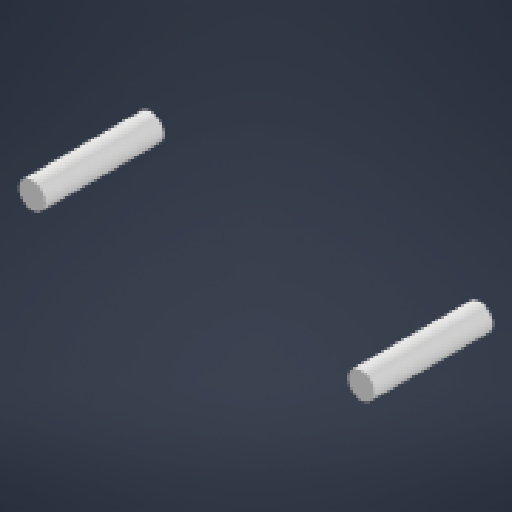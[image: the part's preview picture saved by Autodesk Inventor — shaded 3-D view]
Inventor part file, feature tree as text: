
AUTODESK INVENTOR PART (.ipt)
format: ipt  version: 2024 (Build 280153000, 153)  size: 122,368 bytes
history: native  units: mm
features: other x1, extrude x1, sketch x1
ambient origin geometry x8: Origin, YZ Plane, XZ Plane, XY Plane, X Axis, Y Axis, Z Axis, Center Point
bodies: Body1 (feature_tree)
feature tree (3):
  other  "Sólido1"
  extrude  "Extrusión1"  Depth=18.0mm
  sketch  "Boceto1"  dims[d0=4.0mm d2=124.4mm d3=174.2mm d4=18.0mm d5=0.0mm]
